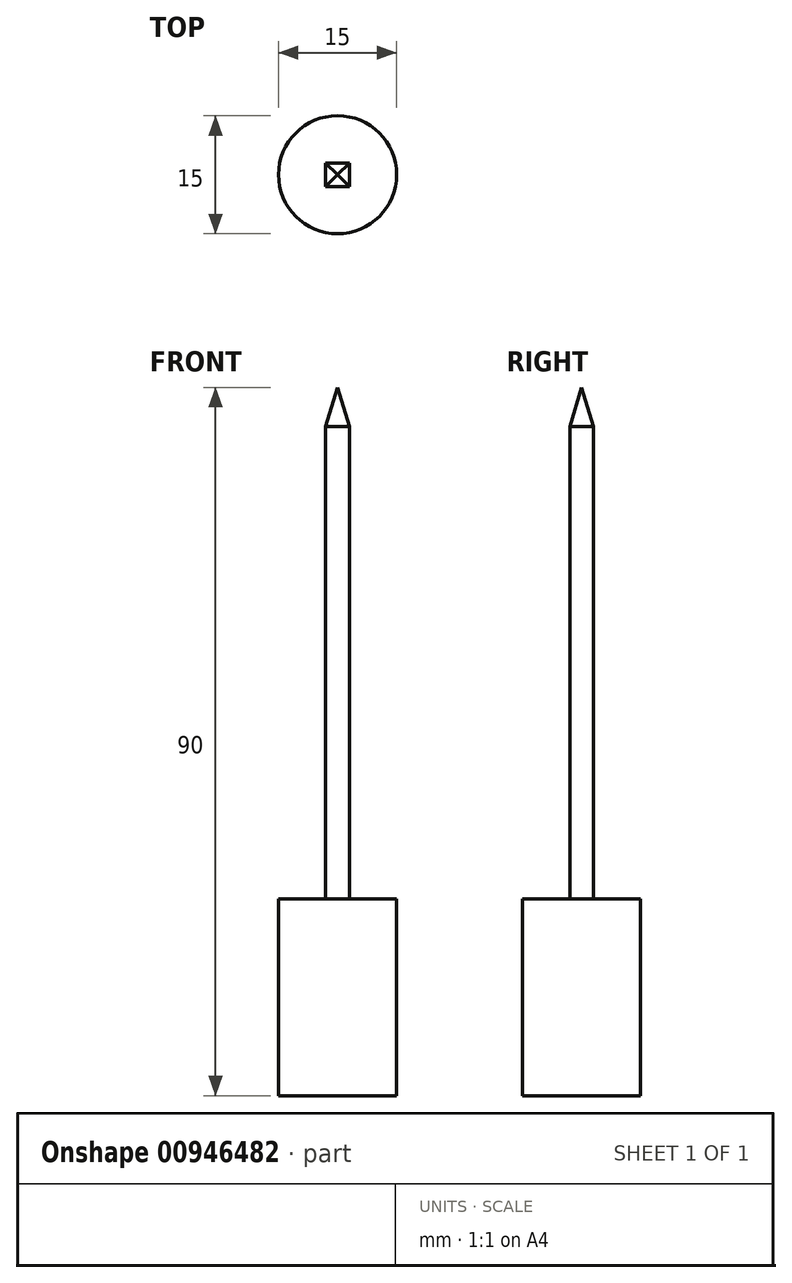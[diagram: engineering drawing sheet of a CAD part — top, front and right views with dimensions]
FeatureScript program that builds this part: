
annotation { "Feature Type Name" : "Feature", "Feature Type Description" : "" }
export const myFeature = defineFeature(function(context is Context, id is Id, definition is map)
    precondition{}
    {
        {
            var Q0;
            Q0=qCreatedBy(makeId("Top.planeOp"),FACE);
            var sketch = newSketch(context, id + "F0", { "sketchPlane" : qUnion([Q0])});
            skCircle(sketch, "E0", {"center": v(0, 0) * mm, "radius": 7.5 * mm});
            skSolve(sketch);
        }
        {
            var Q0;
            Q0 = qSketchRegion(id + "F0", true);
            extrude(context, id + "F1", {"entities" : qUnion([Q0]), "depth" : 25 * mm, "offsetDistance" : 25 * mm});
        }
        {
            var Q0;
            Q0=makeQuery(id+"F1.opExtrude","CAP_FACE",FACE,{"disambiguationData":[OSD([sQuery(id+"F0.wireOp",EDGE,"E0")])],"isStart":false});
            var sketch = newSketch(context, id + "F2", { "sketchPlane" : qUnion([Q0])});
            skLineSegment(sketch, "E1.bottom", {"start": v(-1.5, 1.5) * mm, "end": v(1.5, 1.5) * mm});
            skLineSegment(sketch, "E1.top", {"start": v(-1.5, -1.5) * mm, "end": v(1.5, -1.5) * mm});
            skLineSegment(sketch, "E1.left", {"start": v(-1.5, 1.5) * mm, "end": v(-1.5, -1.5) * mm});
            skLineSegment(sketch, "E1.right", {"start": v(1.5, 1.5) * mm, "end": v(1.5, -1.5) * mm});
            skPoint(sketch, "E1.middle", {"position": v(0, 0) * mm});
            skSolve(sketch);
        }
        {
            var Q0;
            Q0=makeQuery(id+"F2.imprint","IMPRINT",FACE,{"disambiguationData":[TD([[makeQuery(id+"F2.imprint","IMPRINT",EDGE,{"derivedFrom":sQuery(id+"F2.wireOp",EDGE,"E1.bottom")}),-1.0]])]});
            extrude(context, id + "F3", {"entities" : qUnion([Q0]), "operationType" : NewBodyOperationType.ADD, "depth" : 60 * mm, "offsetDistance" : 25 * mm});
        }
        {
            var Q0;
            Q0=qCreatedBy(makeId("Front.planeOp"),FACE);
            var sketch = newSketch(context, id + "F4", { "sketchPlane" : qUnion([Q0])});
            skLineSegment(sketch, "E2", {"start": v(0, 0) * mm, "end": v(0, 90) * mm, "construction": true});
            skSolve(sketch);
        }
        {
            var Q1;
            Q1=makeQuery(id+"F3.opExtrude","CAP_FACE",FACE,{"disambiguationData":[OSD([sQuery(id+"F2.wireOp",EDGE,"E1.bottom"),sQuery(id+"F2.wireOp",EDGE,"E1.top"),sQuery(id+"F2.wireOp",EDGE,"E1.left"),sQuery(id+"F2.wireOp",EDGE,"E1.right")])],"isStart":false});
            var Q2;
            Q2=sQuery(id+"F4.wireOp",VERTEX,"E2.end");
            loft(context, id + "F5", {"operationType" : NewBodyOperationType.ADD, "sheetProfilesArray" : [{ "sheetProfileEntities" : qUnion([Q1]) }, { "sheetProfileEntities" : qUnion([Q2]) }]});
        }
    });
